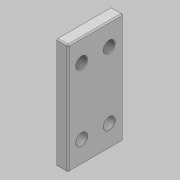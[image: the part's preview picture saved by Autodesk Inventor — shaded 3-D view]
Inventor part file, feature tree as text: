
AUTODESK INVENTOR PART (.ipt)
format: ipt  version: 2018 (Build 220112000, 112)  size: 128,000 bytes
history: native  units: mm
features: other x3, chamfer x2, sketch x2, extrude x1, fillet x1, hole x1
ambient origin geometry x8: Origin, YZ Plane, XZ Plane, XY Plane, X Axis, Y Axis, Z Axis, Center Point
bodies: Body1 (feature_tree)
feature tree (10):
  other  "實體1"
  extrude  "擠出1"  Depth=50.0mm
  fillet  "圓角1"  Radius=100.0mm
  chamfer  "倒角1"  Distance=10.0mm
  hole  "孔1"  [1 undecoded]
  other  "螺紋1"
  other  "螺紋2"
  chamfer  "倒角2"  Distance=1.0mm Angle=45.0deg
  sketch  "草圖1"
  sketch  "草圖2"
note: 1 required parameter value undecoded (feature->parameter linkage not recoverable at this tier; creation-order binding heuristic only, values carry confidence <= 0.55)
